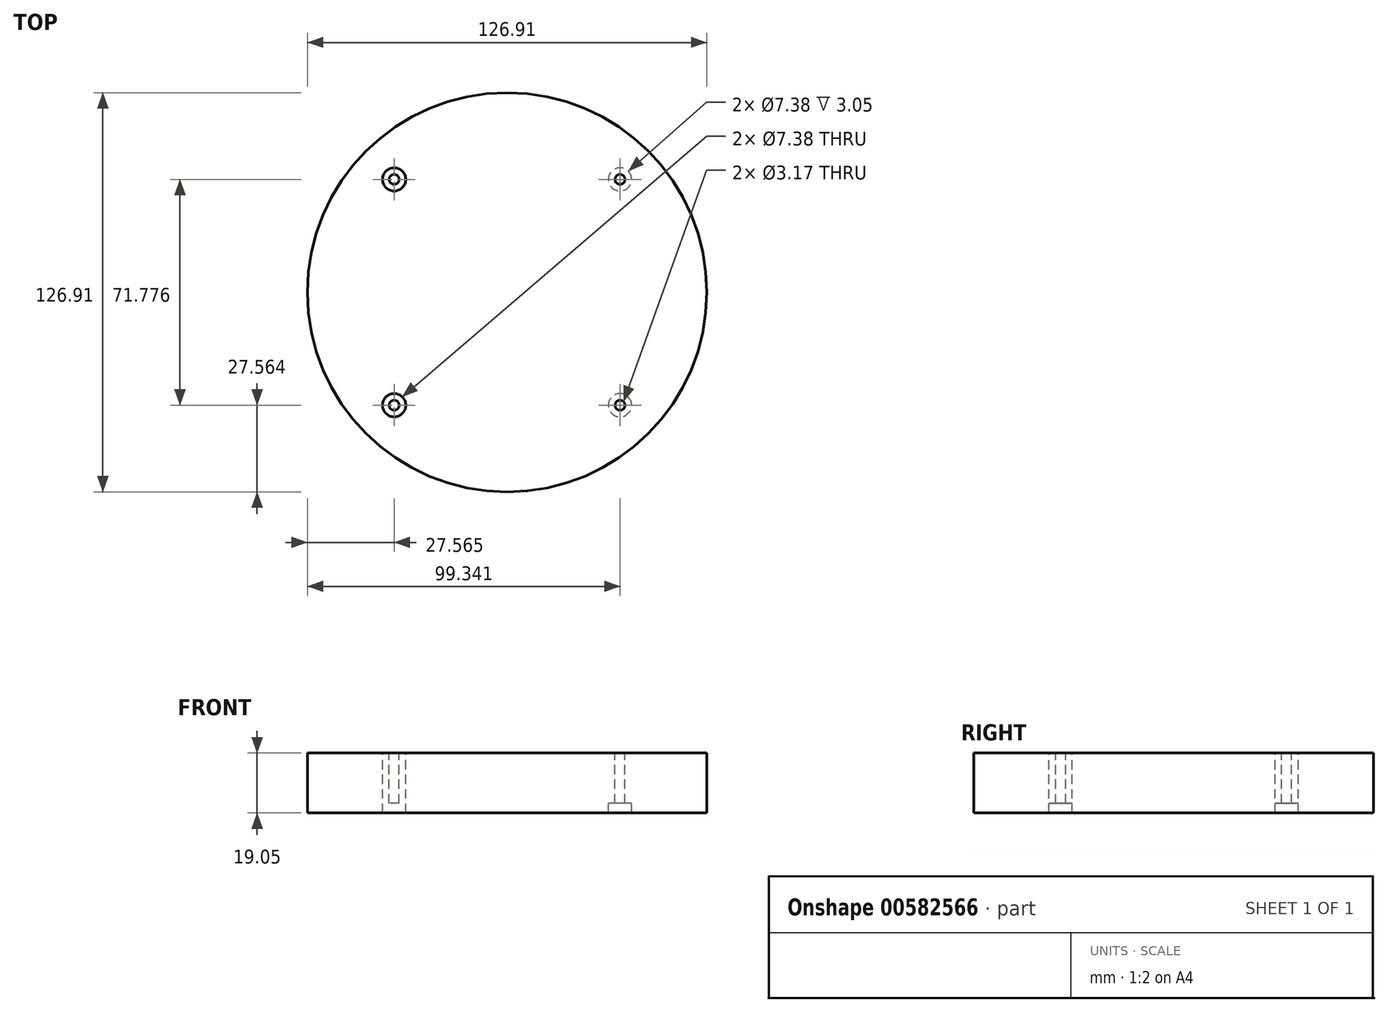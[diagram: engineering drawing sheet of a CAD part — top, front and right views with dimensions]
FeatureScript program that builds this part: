
annotation { "Feature Type Name" : "Feature", "Feature Type Description" : "" }
export const myFeature = defineFeature(function(context is Context, id is Id, definition is map)
    precondition{}
    {
        {
            var Q0;
            Q0=qCreatedBy(makeId("Top.planeOp"),FACE);
            var sketch = newSketch(context, id + "F0", { "sketchPlane" : qUnion([Q0])});
            skCircle(sketch, "E0", {"center": v(77.76, -75.8) * mm, "radius": 63.45 * mm});
            skCircle(sketch, "E1.MirrorC", {"center": v(41.87, -39.92) * mm, "radius": 1.59 * mm});
            skCircle(sketch, "E2.MirrorC", {"center": v(113.65, -111.7) * mm, "radius": 1.59 * mm});
            skCircle(sketch, "E3.MirrorC", {"center": v(41.87, -111.7) * mm, "radius": 1.59 * mm});
            skCircle(sketch, "E4.MirrorC", {"center": v(113.65, -39.92) * mm, "radius": 1.59 * mm});
            skCircle(sketch, "E5", {"center": v(113.65, -39.92) * mm, "radius": 3.69 * mm});
            skCircle(sketch, "E6", {"center": v(41.87, -39.92) * mm, "radius": 3.69 * mm});
            skCircle(sketch, "E7", {"center": v(41.87, -111.7) * mm, "radius": 3.69 * mm});
            skCircle(sketch, "E8", {"center": v(113.65, -111.7) * mm, "radius": 3.69 * mm});
            skSolve(sketch);
        }
        {
            var Q0;
            Q0=makeQuery(id+"F0.imprint","IMPRINT",FACE,{"disambiguationData":[TD([[makeQuery(id+"F0.imprint","IMPRINT",EDGE,{"derivedFrom":sQuery(id+"F0.wireOp",EDGE,"E0")}),1.0]])]});
            extrude(context, id + "F1", {"entities" : qUnion([Q0]), "depth" : -19.05 * mm, "offsetDistance" : 25 * mm});
        }
        {
            var Q0;
            Q0=makeQuery(id+"F0.imprint","IMPRINT",FACE,{"disambiguationData":[TD([[makeQuery(id+"F0.imprint","IMPRINT",EDGE,{"derivedFrom":sQuery(id+"F0.wireOp",EDGE,"E1.MirrorC")}),1.0]])]});
            var Q1;
            Q1=makeQuery(id+"F0.imprint","IMPRINT",FACE,{"disambiguationData":[TD([[makeQuery(id+"F0.imprint","IMPRINT",EDGE,{"derivedFrom":sQuery(id+"F0.wireOp",EDGE,"E4.MirrorC")}),-1.0]])]});
            var Q2;
            Q2=makeQuery(id+"F0.imprint","IMPRINT",FACE,{"disambiguationData":[TD([[makeQuery(id+"F0.imprint","IMPRINT",EDGE,{"derivedFrom":sQuery(id+"F0.wireOp",EDGE,"E2.MirrorC")}),-1.0]])]});
            var Q3;
            Q3=makeQuery(id+"F0.imprint","IMPRINT",FACE,{"disambiguationData":[TD([[makeQuery(id+"F0.imprint","IMPRINT",EDGE,{"derivedFrom":sQuery(id+"F0.wireOp",EDGE,"E3.MirrorC")}),1.0]])]});
            extrude(context, id + "F2", {"entities" : qUnion([Q0, Q1, Q2, Q3]), "operationType" : NewBodyOperationType.ADD, "depth" : -16 * mm, "offsetDistance" : 25 * mm});
        }
    });
